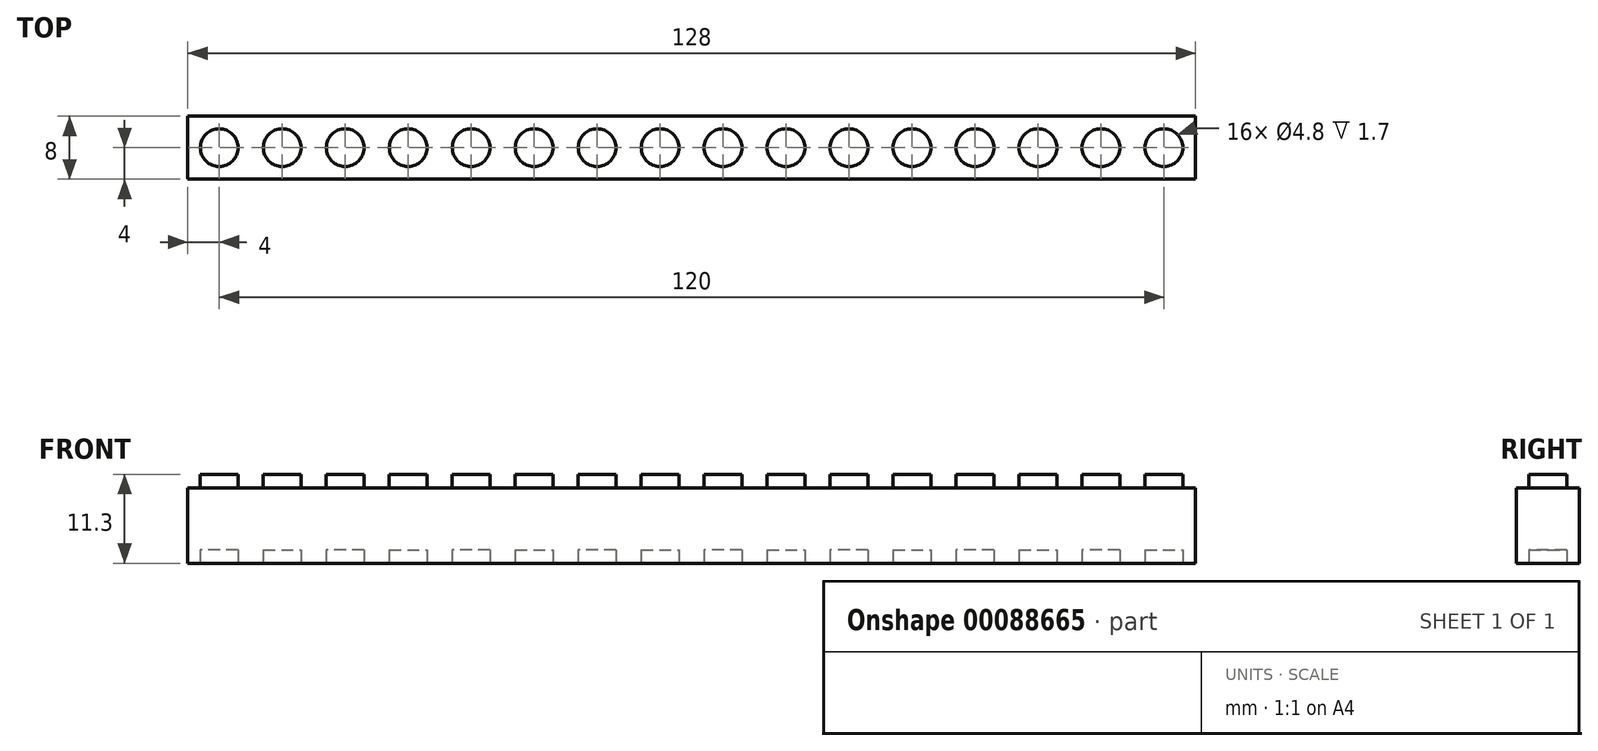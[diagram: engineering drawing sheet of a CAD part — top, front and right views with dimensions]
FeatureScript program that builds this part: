
annotation { "Feature Type Name" : "Feature", "Feature Type Description" : "" }
export const myFeature = defineFeature(function(context is Context, id is Id, definition is map)
    precondition{}
    {
        {
            var Q0;
            Q0=qCreatedBy(makeId("Front.planeOp"),FACE);
            var sketch = newSketch(context, id + "F0", { "sketchPlane" : qUnion([Q0])});
            skLineSegment(sketch, "E0.bottom", {"start": v(-4, 9.6) * mm, "end": v(-2.4, 9.6) * mm});
            skLineSegment(sketch, "E0.top", {"start": v(-4, 0) * mm, "end": v(4, 0) * mm});
            skLineSegment(sketch, "E0.left", {"start": v(-4, 9.6) * mm, "end": v(-4, 0) * mm});
            skLineSegment(sketch, "E0.right", {"start": v(4, 9.6) * mm, "end": v(4, 0) * mm});
            skLineSegment(sketch, "E1.top", {"start": v(-2.4, 11.3) * mm, "end": v(2.4, 11.3) * mm});
            skLineSegment(sketch, "E1.left", {"start": v(-2.4, 9.6) * mm, "end": v(-2.4, 11.3) * mm});
            skLineSegment(sketch, "E1.right", {"start": v(2.4, 9.6) * mm, "end": v(2.4, 11.3) * mm});
            skLineSegment(sketch, "E2", {"start": v(0, 0) * mm, "end": v(0, 24.04) * mm, "construction": true});
            skLineSegment(sketch, "E3.trimOffspring", {"start": v(2.4, 9.6) * mm, "end": v(4, 9.6) * mm});
            skSolve(sketch);
        }
        {
            var Q0;
            Q0=makeQuery(id+"F0.imprint","IMPRINT",FACE,{"disambiguationData":[TD([[makeQuery(id+"F0.imprint","IMPRINT",EDGE,{"derivedFrom":sQuery(id+"F0.wireOp",EDGE,"E0.bottom")}),-1.0]])]});
            extrude(context, id + "F1", {"entities" : qUnion([Q0]), "depth" : 8 * mm});
        }
        {
            var Q0;
            Q0=qCreatedBy(makeId("Top.planeOp"),FACE);
            var Q1;
            Q1=makeQuery(id+"F1.opExtrude","CAP_VERTEX",VERTEX,{"disambiguationData":[OSD([sQuery(id+"F0.wireOp",EDGE,"E1.top"),sQuery(id+"F0.wireOp",EDGE,"E1.right")])],"isStart":true});
            cPlane(context, id + "F2", {"entities" : qUnion([Q0, Q1]), "cplaneType" : CPlaneType.PLANE_POINT, "offset" : 152.4 * mm, "width" : 152.4 * mm, "height" : 152.4 * mm});
        }
        {
            var Q0;
            Q0=qCreatedBy(id+"F2.planeOp",FACE);
            var sketch = newSketch(context, id + "F3", { "sketchPlane" : qUnion([Q0])});
            skLineSegment(sketch, "E4.0", {"start": v(-4, -8) * mm, "end": v(-4, 0) * mm});
            skLineSegment(sketch, "E5.0", {"start": v(4, -8) * mm, "end": v(4, 0) * mm});
            skLineSegment(sketch, "E6", {"start": v(-4, 0) * mm, "end": v(4, 0) * mm});
            skLineSegment(sketch, "E7", {"start": v(-4, -8) * mm, "end": v(4, -8) * mm});
            skLineSegment(sketch, "E8", {"start": v(-4, 0) * mm, "end": v(4, -8) * mm, "construction": true});
            skLineSegment(sketch, "E9", {"start": v(-4, -8) * mm, "end": v(4, 0) * mm, "construction": true});
            skCircle(sketch, "E10", {"center": v(0, -4) * mm, "radius": 2.4 * mm});
            skSolve(sketch);
        }
        {
            var Q0;
            Q0=qSketchRegion(id+"F3",true);
            var Q1;
            Q1=makeQuery(id+"F1.opExtrude","SWEPT_FACE",FACE,{"disambiguationData":[OSD([sQuery(id+"F0.wireOp",EDGE,"E0.bottom")])]});
            extrude(context, id + "F4", {"entities" : qUnion([Q0]), "operationType" : NewBodyOperationType.REMOVE, "endBound" : BoundingType.UP_TO_SURFACE, "oppositeDirection" : true, "endBoundEntityFace" : qUnion([Q1]), "depth" : 25.4 * mm});
        }
        {
            var Q0;
            Q0=qCreatedBy(makeId("Top.planeOp"),FACE);
            var sketch = newSketch(context, id + "F5", { "sketchPlane" : qUnion([Q0])});
            skCircle(sketch, "E11.0", {"center": v(0, -4) * mm, "radius": 2.4 * mm});
            skSolve(sketch);
        }
        {
            var Q0;
            Q0=makeQuery(id+"F5.imprint","IMPRINT",FACE,{"disambiguationData":[TD([[makeQuery(id+"F5.imprint","IMPRINT",EDGE,{"derivedFrom":sQuery(id+"F5.wireOp",EDGE,"E11.0")}),1.0]])]});
            extrude(context, id + "F6", {"entities" : qUnion([Q0]), "operationType" : NewBodyOperationType.REMOVE, "depth" : 1.7 * mm});
        }
        {
            var Q0;
            Q0=qCreatedBy(makeId("Right.planeOp"),FACE);
            var Q1;
            Q1=makeQuery(id+"F1.opExtrude","CAP_VERTEX",VERTEX,{"disambiguationData":[OSD([sQuery(id+"F0.wireOp",EDGE,"E0.right"),sQuery(id+"F0.wireOp",EDGE,"E3.trimOffspring")])],"isStart":false});
            cPlane(context, id + "F7", {"entities" : qUnion([Q0, Q1]), "cplaneType" : CPlaneType.PLANE_POINT, "offset" : 152.4 * mm, "width" : 152.4 * mm, "height" : 152.4 * mm});
        }
        {
            var Q0;
            Q0=makeQuery(id+"F1.opExtrude","SWEPT_BODY",BODY,{"disambiguationData":[OSD([sQuery(id+"F0.wireOp",EDGE,"E0.bottom"),sQuery(id+"F0.wireOp",EDGE,"E0.top"),sQuery(id+"F0.wireOp",EDGE,"E0.left"),sQuery(id+"F0.wireOp",EDGE,"E0.right"),sQuery(id+"F0.wireOp",EDGE,"E1.top"),sQuery(id+"F0.wireOp",EDGE,"E1.left"),sQuery(id+"F0.wireOp",EDGE,"E1.right"),sQuery(id+"F0.wireOp",EDGE,"E3.trimOffspring")])]});
            var Q1;
            Q1=qCreatedBy(id+"F7.planeOp",FACE);
            mirror(context, id + "F8", {"operationType" : NewBodyOperationType.ADD, "entities" : qUnion([Q0]), "mirrorPlane" : qUnion([Q1])});
        }
        {
            var Q0;
            Q0=qCreatedBy(id+"F7.planeOp",FACE);
            var Q1;
            Q1=makeQuery(id+"F8.opPattern","COPY",VERTEX,{"derivedFrom":makeQuery(id+"F1.opExtrude","CAP_VERTEX",VERTEX,{"disambiguationData":[OSD([sQuery(id+"F0.wireOp",EDGE,"E0.bottom"),sQuery(id+"F0.wireOp",EDGE,"E0.left")])],"isStart":false}),"instanceName":"1"});
            cPlane(context, id + "F9", {"entities" : qUnion([Q0, Q1]), "cplaneType" : CPlaneType.PLANE_POINT, "offset" : 152.4 * mm, "width" : 152.4 * mm, "height" : 152.4 * mm});
        }
        {
            var Q0;
            Q0=makeQuery(id+"F1.opExtrude","SWEPT_BODY",BODY,{"disambiguationData":[OSD([sQuery(id+"F0.wireOp",EDGE,"E0.bottom"),sQuery(id+"F0.wireOp",EDGE,"E0.top"),sQuery(id+"F0.wireOp",EDGE,"E0.left"),sQuery(id+"F0.wireOp",EDGE,"E0.right"),sQuery(id+"F0.wireOp",EDGE,"E1.top"),sQuery(id+"F0.wireOp",EDGE,"E1.left"),sQuery(id+"F0.wireOp",EDGE,"E1.right"),sQuery(id+"F0.wireOp",EDGE,"E3.trimOffspring")])]});
            var Q1;
            Q1=qCreatedBy(id+"F9.planeOp",FACE);
            mirror(context, id + "F10", {"operationType" : NewBodyOperationType.ADD, "entities" : qUnion([Q0]), "mirrorPlane" : qUnion([Q1])});
        }
        {
            var Q0;
            Q0=qCreatedBy(makeId("Right.planeOp"),FACE);
            var Q1;
            Q1=makeQuery(id+"F10.opPattern","COPY",VERTEX,{"derivedFrom":makeQuery(id+"F1.opExtrude","CAP_VERTEX",VERTEX,{"disambiguationData":[OSD([sQuery(id+"F0.wireOp",EDGE,"E0.bottom"),sQuery(id+"F0.wireOp",EDGE,"E0.left")])],"isStart":false}),"instanceName":"1"});
            cPlane(context, id + "F11", {"entities" : qUnion([Q0, Q1]), "cplaneType" : CPlaneType.PLANE_POINT, "offset" : 152.4 * mm, "width" : 152.4 * mm, "height" : 152.4 * mm});
        }
        {
            var Q0;
            Q0=makeQuery(id+"F1.opExtrude","SWEPT_BODY",BODY,{"disambiguationData":[OSD([sQuery(id+"F0.wireOp",EDGE,"E0.bottom"),sQuery(id+"F0.wireOp",EDGE,"E0.top"),sQuery(id+"F0.wireOp",EDGE,"E0.left"),sQuery(id+"F0.wireOp",EDGE,"E0.right"),sQuery(id+"F0.wireOp",EDGE,"E1.top"),sQuery(id+"F0.wireOp",EDGE,"E1.left"),sQuery(id+"F0.wireOp",EDGE,"E1.right"),sQuery(id+"F0.wireOp",EDGE,"E3.trimOffspring")])]});
            var Q1;
            Q1=qCreatedBy(id+"F11.planeOp",FACE);
            mirror(context, id + "F12", {"operationType" : NewBodyOperationType.ADD, "entities" : qUnion([Q0]), "mirrorPlane" : qUnion([Q1])});
        }
        {
            var Q0;
            Q0=makeQuery(id+"F1.opExtrude","SWEPT_BODY",BODY,{"disambiguationData":[OSD([sQuery(id+"F0.wireOp",EDGE,"E0.bottom"),sQuery(id+"F0.wireOp",EDGE,"E0.top"),sQuery(id+"F0.wireOp",EDGE,"E0.left"),sQuery(id+"F0.wireOp",EDGE,"E0.right"),sQuery(id+"F0.wireOp",EDGE,"E1.top"),sQuery(id+"F0.wireOp",EDGE,"E1.left"),sQuery(id+"F0.wireOp",EDGE,"E1.right"),sQuery(id+"F0.wireOp",EDGE,"E3.trimOffspring")])]});
            var Q1;
            Q1=makeQuery(id+"F12.opPattern","COPY",FACE,{"derivedFrom":makeQuery(id+"F1.opExtrude","SWEPT_FACE",FACE,{"disambiguationData":[OSD([sQuery(id+"F0.wireOp",EDGE,"E0.left")])]}),"instanceName":"1"});
            mirror(context, id + "F13", {"operationType" : NewBodyOperationType.ADD, "entities" : qUnion([Q0]), "mirrorPlane" : qUnion([Q1])});
        }
    });
